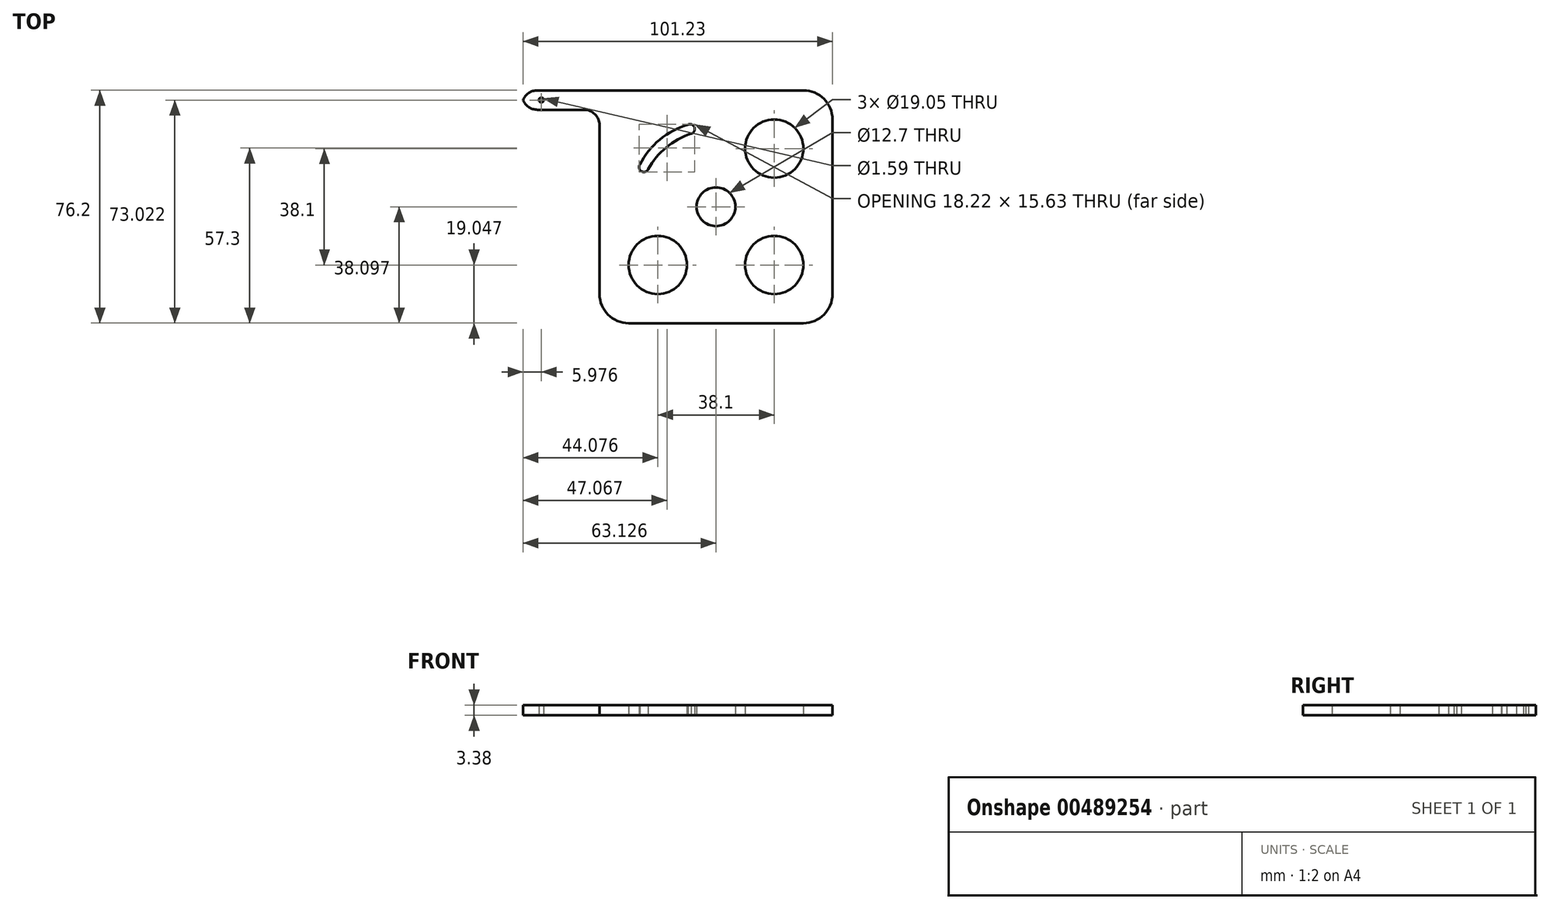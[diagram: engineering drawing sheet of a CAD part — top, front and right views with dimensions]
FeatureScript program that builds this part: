
annotation { "Feature Type Name" : "Feature", "Feature Type Description" : "" }
export const myFeature = defineFeature(function(context is Context, id is Id, definition is map)
    precondition{}
    {
        {
            var Q0;
            Q0=qCreatedBy(makeId("Top.planeOp"),FACE);
            var sketch = newSketch(context, id + "F0", { "sketchPlane" : qUnion([Q0])});
            skLineSegment(sketch, "E0.bottom", {"start": v(-45.51, 40.7) * mm, "end": v(30.69, 40.7) * mm});
            skLineSegment(sketch, "E0.top", {"start": v(-45.51, -35.5) * mm, "end": v(30.69, -35.5) * mm});
            skLineSegment(sketch, "E0.right", {"start": v(30.69, 40.7) * mm, "end": v(30.69, -35.5) * mm});
            skPoint(sketch, "E0.middle", {"position": v(-7.41, 2.6) * mm});
            skPoint(sketch, "E1", {"position": v(11.64, 21.65) * mm});
            skPoint(sketch, "E2", {"position": v(11.64, -16.45) * mm});
            skPoint(sketch, "E3", {"position": v(-26.46, -16.45) * mm});
            skPoint(sketch, "E4", {"position": v(0, 0) * mm});
            skLineSegment(sketch, "E5", {"start": v(-45.51, 40.7) * mm, "end": v(-45.51, -35.5) * mm});
            skLineSegment(sketch, "E6.bottom", {"start": v(-45.51, 40.7) * mm, "end": v(-70.91, 40.7) * mm});
            skLineSegment(sketch, "E6.top", {"start": v(-45.51, 34.35) * mm, "end": v(-70.91, 34.35) * mm});
            skLineSegment(sketch, "E6.left", {"start": v(-45.51, 40.7) * mm, "end": v(-45.51, 34.35) * mm});
            skLineSegment(sketch, "E6.right", {"start": v(-70.91, 40.7) * mm, "end": v(-70.91, 34.35) * mm});
            skPoint(sketch, "E7", {"position": v(-64.56, 37.52) * mm});
            skCircle(sketch, "E8", {"center": v(-15.94, 28.03) * mm, "radius": 1.59 * mm});
            skArc(sketch, "E9", {"start": v(-32.36, 16.4) * mm, "mid": v(-31.77, 14.17) * mm, "end": v(-29.58, 14.89) * mm});
            skArc(sketch, "E10", {"start": v(-15.59, 26.48) * mm, "mid": v(-14.51, 28.71) * mm, "end": v(-16.92, 29.28) * mm});
            skArc(sketch, "E11", {"start": v(-15.59, 26.48) * mm, "mid": v(-23.68, 22.02) * mm, "end": v(-29.58, 14.89) * mm});
            skArc(sketch, "E12", {"start": v(-16.58, 29.48) * mm, "mid": v(-25.8, 24.55) * mm, "end": v(-32.36, 16.4) * mm});
            skSolve(sketch);
        }
        {
            var Q0;
            Q0=makeQuery(id+"F0.imprint","IMPRINT",FACE,{"disambiguationData":[TD([[makeQuery(id+"F0.imprint","IMPRINT",EDGE,{"derivedFrom":sQuery(id+"F0.wireOp",EDGE,"E0.bottom")}),-1.0]])]});
            var Q1;
            {var subQ1=sQuery(id+"F0.wireOp",EDGE,"hBzWq3Zm-ojhb-zLjC-NG0J-HgbkhjsHaN26");Q1=makeQuery(id+"F0.imprint","IMPRINT",FACE,{"disambiguationData":[TD([[makeQuery(id+"F0.imprint","IMPRINT",EDGE,{"derivedFrom":subQ1}),-1.0]])]});}
            var Q2;
            Q2=makeQuery(id+"F0.imprint","IMPRINT",FACE,{"disambiguationData":[TD([[makeQuery(id+"F0.imprint","IMPRINT",EDGE,{"derivedFrom":sQuery(id+"F0.wireOp",EDGE,"E6.bottom")}),1.0]])]});
            extrude(context, id + "F1", {"entities" : qUnion([Q0, Q1, Q2]), "depth" : 3.38 * mm, "offsetDistance" : 25.4 * mm});
        }
        {
            var Q0;
            Q0=sQuery(id+"F0.wireOp",VERTEX,"E0.middle");
            var Q1;
            Q1=makeQuery(id+"F1.opExtrude","SWEPT_BODY",BODY,{"disambiguationData":[OSD([sQuery(id+"F0.wireOp",EDGE,"E0.bottom"),sQuery(id+"F0.wireOp",EDGE,"E0.top"),sQuery(id+"F0.wireOp",EDGE,"E0.left"),sQuery(id+"F0.wireOp",EDGE,"E0.right")])]});
            hole(context, id + "F2", {"style" : HoleStyle.SIMPLE, "endStyle" : HoleEndStyle.THROUGH, "oppositeDirection" : true, "holeDiameter" : 12.7 * mm, "isTappedThrough" : true, "tappedDepth" : 12.7 * mm, "tapClearance" : 3, "startFromSketch" : true, "locations" : qUnion([Q0]), "scope" : qUnion([Q1])});
        }
        {
            var Q0;
            Q0=sQuery(id+"F0.wireOp",VERTEX,"E1");
            var Q1;
            Q1=sQuery(id+"F0.wireOp",VERTEX,"E2");
            var Q2;
            Q2=sQuery(id+"F0.wireOp",VERTEX,"E3");
            var Q3;
            Q3=makeQuery(id+"F1.opExtrude","SWEPT_BODY",BODY,{"disambiguationData":[OSD([sQuery(id+"F0.wireOp",EDGE,"E0.bottom"),sQuery(id+"F0.wireOp",EDGE,"E0.top"),sQuery(id+"F0.wireOp",EDGE,"E0.left"),sQuery(id+"F0.wireOp",EDGE,"E0.right")])]});
            hole(context, id + "F3", {"style" : HoleStyle.SIMPLE, "endStyle" : HoleEndStyle.THROUGH, "oppositeDirection" : true, "holeDiameter" : 19.05 * mm, "isTappedThrough" : true, "tappedDepth" : 12.7 * mm, "tapClearance" : 3, "startFromSketch" : true, "locations" : qUnion([Q0, Q1, Q2]), "scope" : qUnion([Q3])});
        }
        {
            var Q0;
            Q0=sQuery(id+"F0.wireOp",VERTEX,"E7");
            var Q1;
            Q1=makeQuery(id+"F1.opExtrude","SWEPT_BODY",BODY,{"disambiguationData":[OSD([sQuery(id+"F0.wireOp",EDGE,"E0.bottom"),sQuery(id+"F0.wireOp",EDGE,"E0.top"),sQuery(id+"F0.wireOp",EDGE,"E0.right"),sQuery(id+"F0.wireOp",EDGE,"E5"),sQuery(id+"F0.wireOp",EDGE,"E6.bottom"),sQuery(id+"F0.wireOp",EDGE,"E6.top"),sQuery(id+"F0.wireOp",EDGE,"E6.right")])]});
            hole(context, id + "F4", {"style" : HoleStyle.SIMPLE, "endStyle" : HoleEndStyle.THROUGH, "oppositeDirection" : true, "holeDiameter" : 1.59 * mm, "isTappedThrough" : true, "tappedDepth" : 12.7 * mm, "tapClearance" : 3, "startFromSketch" : true, "locations" : qUnion([Q0]), "scope" : qUnion([Q1])});
        }
        {
            var Q0;
            Q0=makeQuery(id+"F1.opExtrude","SWEPT_EDGE",EDGE,{"disambiguationData":[OSD([sQuery(id+"F0.wireOp",EDGE,"E0.top"),sQuery(id+"F0.wireOp",EDGE,"E0.right")])]});
            var Q1;
            Q1=makeQuery(id+"F1.opExtrude","SWEPT_EDGE",EDGE,{"disambiguationData":[OSD([sQuery(id+"F0.wireOp",EDGE,"E0.top"),sQuery(id+"F0.wireOp",EDGE,"E5")])]});
            var Q2;
            Q2=makeQuery(id+"F1.opExtrude","SWEPT_EDGE",EDGE,{"disambiguationData":[OSD([sQuery(id+"F0.wireOp",EDGE,"E0.bottom"),sQuery(id+"F0.wireOp",EDGE,"E0.right")])]});
            fillet(context, id + "F5", {"entities" : qUnion([Q0, Q1, Q2]), "radius" : 9.52 * mm, "tangentPropagation" : true, "allowEdgeOverflow" : false});
        }
        {
            var Q0;
            Q0=makeQuery(id+"F1.opExtrude","SWEPT_EDGE",EDGE,{"disambiguationData":[OSD([sQuery(id+"F0.wireOp",EDGE,"E6.bottom"),sQuery(id+"F0.wireOp",EDGE,"E6.right")])]});
            var Q1;
            Q1=makeQuery(id+"F1.opExtrude","SWEPT_EDGE",EDGE,{"disambiguationData":[OSD([sQuery(id+"F0.wireOp",EDGE,"E6.top"),sQuery(id+"F0.wireOp",EDGE,"E6.right")])]});
            fillet(context, id + "F6", {"entities" : qUnion([Q0, Q1]), "radius" : 5.08 * mm, "tangentPropagation" : true, "allowEdgeOverflow" : false});
        }
        {
            var Q0;
            Q0=makeQuery(id+"F1.opExtrude","SWEPT_EDGE",EDGE,{"disambiguationData":[OSD([sQuery(id+"F0.wireOp",EDGE,"E5"),sQuery(id+"F0.wireOp",EDGE,"E6.top"),sQuery(id+"F0.wireOp",EDGE,"E6.left")])]});
            fillet(context, id + "F7", {"entities" : qUnion([Q0]), "radius" : 5.08 * mm, "tangentPropagation" : true, "allowEdgeOverflow" : false});
        }
    });
